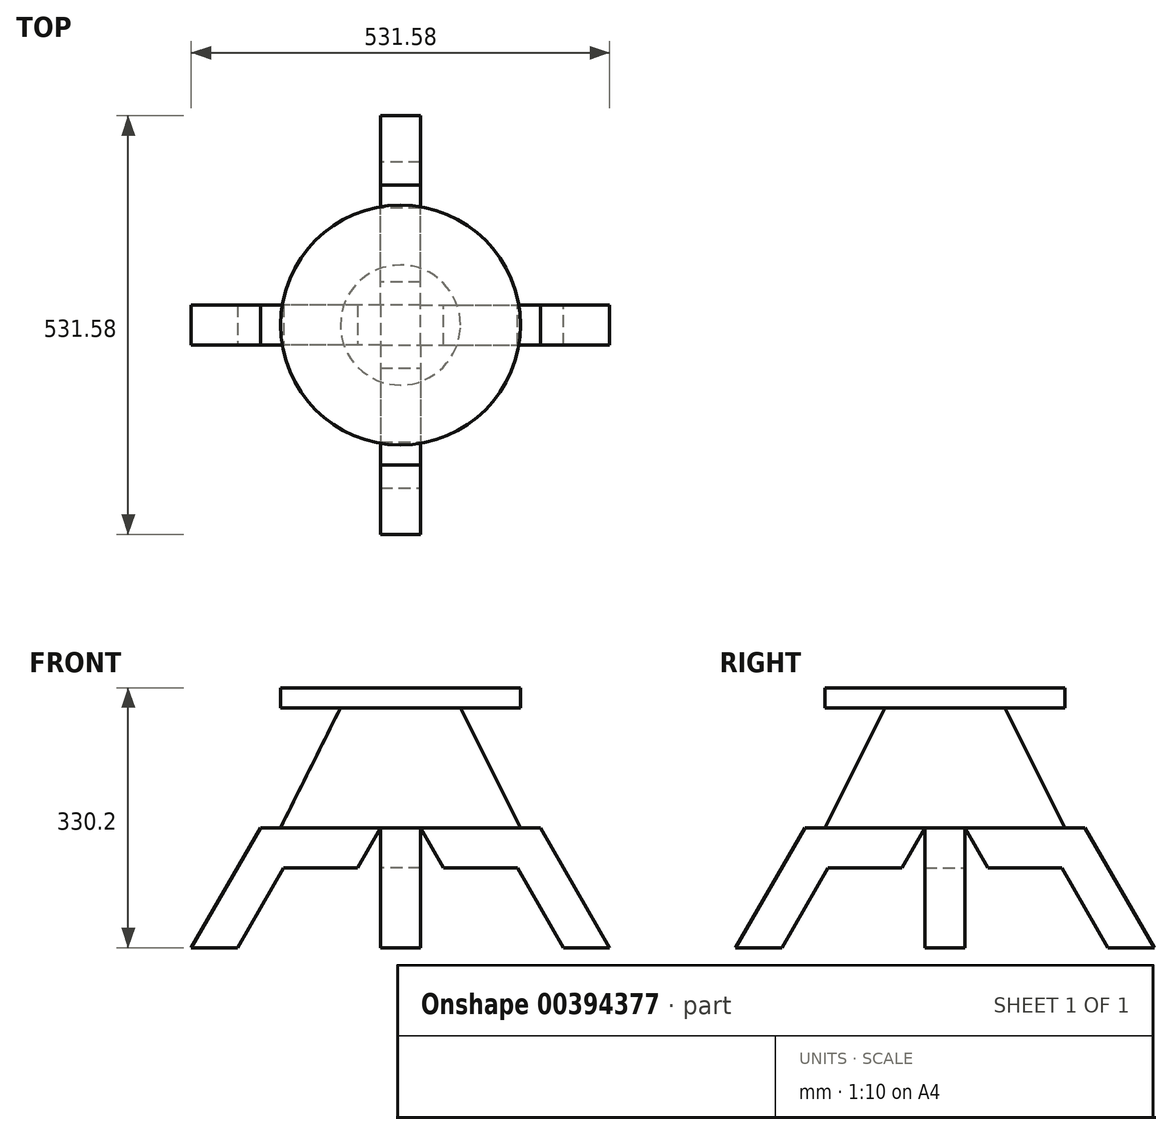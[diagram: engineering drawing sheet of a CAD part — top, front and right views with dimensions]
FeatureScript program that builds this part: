
annotation { "Feature Type Name" : "Feature", "Feature Type Description" : "" }
export const myFeature = defineFeature(function(context is Context, id is Id, definition is map)
    precondition{}
    {
        {
            var Q0;
            Q0=qCreatedBy(makeId("Front.planeOp"),FACE);
            var sketch = newSketch(context, id + "F0", { "sketchPlane" : qUnion([Q0])});
            skLineSegment(sketch, "E0.bottom", {"start": v(0, 0) * mm, "end": v(-152.4, 0) * mm});
            skLineSegment(sketch, "E0.top", {"start": v(0, 25.4) * mm, "end": v(-152.4, 25.4) * mm});
            skLineSegment(sketch, "E0.left", {"start": v(0, 0) * mm, "end": v(0, 25.4) * mm});
            skLineSegment(sketch, "E0.right", {"start": v(-152.4, 0) * mm, "end": v(-152.4, 25.4) * mm});
            skLineSegment(sketch, "E1.bottom", {"start": v(-152.4, 25.4) * mm, "end": v(-127, 25.4) * mm});
            skLineSegment(sketch, "E1.top", {"start": v(-152.4, 101.6) * mm, "end": v(-127, 101.6) * mm});
            skLineSegment(sketch, "E1.left", {"start": v(-152.4, 25.4) * mm, "end": v(-152.4, 101.6) * mm});
            skLineSegment(sketch, "E1.right", {"start": v(-127, 25.4) * mm, "end": v(-127, 101.6) * mm});
            skSolve(sketch);
        }
        {
            var Q0;
            Q0=makeQuery(id+"F0.imprint","IMPRINT",FACE,{"disambiguationData":[TD([[makeQuery(id+"F0.imprint","IMPRINT",EDGE,{"derivedFrom":sQuery(id+"F0.wireOp",EDGE,"E1.bottom")}),1.0]])]});
            var Q1;
            Q1=makeQuery(id+"F0.imprint","IMPRINT",FACE,{"disambiguationData":[TD([[makeQuery(id+"F0.imprint","IMPRINT",EDGE,{"derivedFrom":sQuery(id+"F0.wireOp",EDGE,"E0.bottom")}),-1.0]])]});
            var Q2;
            Q2=sQuery(id+"F0.wireOp",EDGE,"E0.left");
            revolve(context, id + "F1", {"entities" : qUnion([Q0, Q1]), "axis" : qUnion([Q2]), "revolveType" : RevolveType.FULL});
        }
        {
            var Q0;
            Q0=qCreatedBy(makeId("Front.planeOp"),FACE);
            cPlane(context, id + "F2", {"entities" : qUnion([Q0]), "cplaneType" : CPlaneType.OFFSET, "offset" : 152.4 * mm, "width" : 152.4 * mm, "height" : 152.4 * mm});
        }
        {
            var Q0;
            Q0=qCreatedBy(id+"F2.planeOp",FACE);
            var sketch = newSketch(context, id + "F3", { "sketchPlane" : qUnion([Q0])});
            skCircle(sketch, "E2", {"center": v(0, 50.8) * mm, "radius": 6.35 * mm});
            skSolve(sketch);
        }
        {
            var Q0;
            Q0=makeQuery(id+"F3.imprint","IMPRINT",FACE,{"disambiguationData":[TD([[makeQuery(id+"F3.imprint","IMPRINT",EDGE,{"derivedFrom":sQuery(id+"F3.wireOp",EDGE,"E2")}),1.0]])]});
            extrude(context, id + "F4", {"entities" : qUnion([Q0]), "operationType" : NewBodyOperationType.REMOVE, "oppositeDirection" : true, "depth" : 50.8 * mm});
        }
        {
            var Q0;
            Q0=makeQuery(id+"F1.opRevolve","SWEPT_FACE",FACE,{"disambiguationData":[OSD([sQuery(id+"F0.wireOp",EDGE,"E0.bottom")])]});
            var sketch = newSketch(context, id + "F5", { "sketchPlane" : qUnion([Q0])});
            skCircle(sketch, "E3", {"center": v(0, 0) * mm, "radius": 76.2 * mm});
            skSolve(sketch);
        }
        {
            var Q0;
            Q0=makeQuery(id+"F5.imprint","IMPRINT",FACE,{"disambiguationData":[TD([[makeQuery(id+"F5.imprint","IMPRINT",EDGE,{"derivedFrom":sQuery(id+"F5.wireOp",EDGE,"E3")}),-1.0]])]});
            cPlane(context, id + "F6", {"entities" : qUnion([Q0]), "cplaneType" : CPlaneType.OFFSET, "offset" : 152.4 * mm, "width" : 152.4 * mm, "height" : 152.4 * mm});
        }
        {
            var Q0;
            Q0=qCreatedBy(id+"F6.planeOp",FACE);
            var sketch = newSketch(context, id + "F7", { "sketchPlane" : qUnion([Q0])});
            skCircle(sketch, "E4", {"center": v(0, 0) * mm, "radius": 152.4 * mm});
            skSolve(sketch);
        }
        {
            var Q1;
            Q1=makeQuery(id+"F5.imprint","IMPRINT",FACE,{"disambiguationData":[TD([[makeQuery(id+"F5.imprint","IMPRINT",EDGE,{"derivedFrom":sQuery(id+"F5.wireOp",EDGE,"E3")}),1.0]])]});
            var Q2;
            Q2=makeQuery(id+"F7.imprint","IMPRINT",FACE,{"disambiguationData":[TD([[makeQuery(id+"F7.imprint","IMPRINT",EDGE,{"derivedFrom":sQuery(id+"F7.wireOp",EDGE,"E4")}),1.0]])]});
            loft(context, id + "F8", {"operationType" : NewBodyOperationType.ADD, "sheetProfilesArray" : [{ "sheetProfileEntities" : qUnion([Q1]) }, { "sheetProfileEntities" : qUnion([Q2]) }]});
        }
        {
            var Q0;
            Q0=qCreatedBy(makeId("Right.planeOp"),FACE);
            var sketch = newSketch(context, id + "F9", { "sketchPlane" : qUnion([Q0])});
            skPoint(sketch, "E5", {"position": v(0, -152.4) * mm});
            skLineSegment(sketch, "E6", {"start": v(25.4, -152.4) * mm, "end": v(177.8, -152.4) * mm});
            skLineSegment(sketch, "E7", {"start": v(177.8, -152.4) * mm, "end": v(265.79, -304.8) * mm});
            skLineSegment(sketch, "E8", {"start": v(265.79, -304.8) * mm, "end": v(207.13, -304.8) * mm});
            skLineSegment(sketch, "E9", {"start": v(25.4, -152.4) * mm, "end": v(54.73, -203.2) * mm});
            skLineSegment(sketch, "E10", {"start": v(54.73, -203.2) * mm, "end": v(148.47, -203.2) * mm});
            skLineSegment(sketch, "E11", {"start": v(148.47, -203.2) * mm, "end": v(207.13, -304.8) * mm});
            skSolve(sketch);
        }
        {
            var Q0;
            Q0=makeQuery(id+"F9.imprint","IMPRINT",FACE,{"disambiguationData":[TD([[makeQuery(id+"F9.imprint","IMPRINT",EDGE,{"derivedFrom":sQuery(id+"F9.wireOp",EDGE,"E6")}),-1.0]])]});
            extrude(context, id + "F10", {"entities" : qUnion([Q0]), "endBound" : BoundingType.SYMMETRIC, "depth" : 50.8 * mm});
        }
        {
            var Q0;
            Q0=makeQuery(id+"F10.opExtrude","SWEPT_BODY",BODY,{"disambiguationData":[OSD([sQuery(id+"F9.wireOp",EDGE,"E6"),sQuery(id+"F9.wireOp",EDGE,"E7"),sQuery(id+"F9.wireOp",EDGE,"E8"),sQuery(id+"F9.wireOp",EDGE,"E9"),sQuery(id+"F9.wireOp",EDGE,"E10"),sQuery(id+"F9.wireOp",EDGE,"E11")])]});
            var Q1;
            Q1=makeQuery(id+"F8.opLoft","SWEPT_FACE",FACE,{"disambiguationData":[OSD([sQuery(id+"F5.wireOp",EDGE,"E3"),sQuery(id+"F7.wireOp",EDGE,"E4")])]});
            circularPattern(context, id + "F11", {"operationType" : NewBodyOperationType.ADD, "entities" : qUnion([Q0]), "axis" : qUnion([Q1]), "angle" : 360 * degree, "instanceCount" : 4, "equalSpace" : true});
        }
    });
